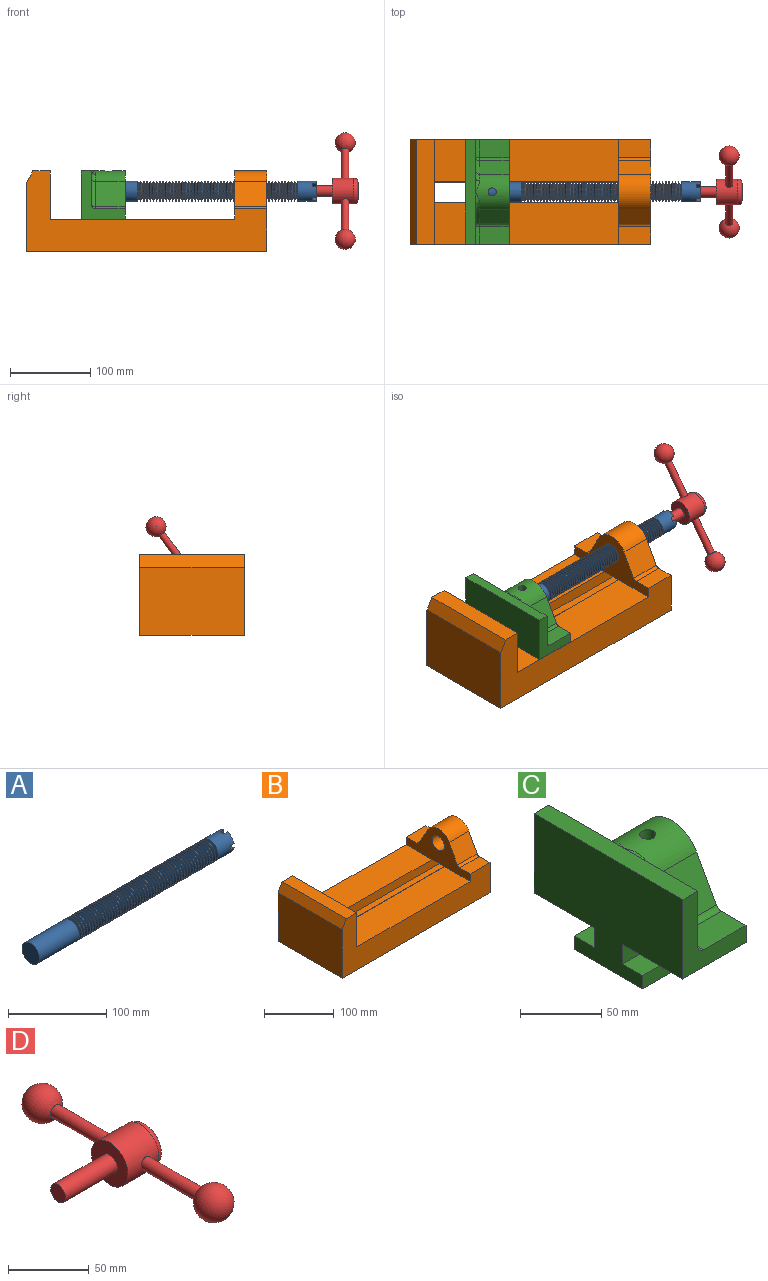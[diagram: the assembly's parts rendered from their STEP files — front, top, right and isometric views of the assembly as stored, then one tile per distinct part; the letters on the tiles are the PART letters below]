
ASSEMBLY  parts=4 mates=3
PART A: 220 faces, bbox 280x25x25 mm
  f0: cylinder r=12.5mm len=25mm, axis (-1,0,0), area 1705.7mm2, adj f1,f2,f3,f54,f57,f208,f209,f210
  f1: plane 9.75x9.75mm, normal (1,0,0), area 59.1mm2, adj f0,f4,f210,f213
  f2: plane 9.75x9.75mm, normal (1,0,0), area 59.1mm2, adj f0,f4,f212,f216
  f3: plane 9.75x9.75mm, normal (1,0,0), area 59.1mm2, adj f0,f4,f209,f218
  f4: cylinder r=6.5mm len=25mm, axis (1,0,0), area 918.4mm2, adj f1,f2,f3,f54,f207,f208,f209,f210
  f5: cylinder r=12.5mm len=25mm, axis (-1,0,0), area 39.3mm2, adj f199,f204
  f6: cylinder r=12.5mm len=25mm, axis (-1,0,0), area 39.3mm2, adj f196,f201
  f7: cylinder r=12.5mm len=25mm, axis (-1,0,0), area 39.3mm2, adj f193,f198
  f8: cylinder r=12.5mm len=25mm, axis (-1,0,0), area 39.3mm2, adj f190,f195
  f9: cylinder r=12.5mm len=25mm, axis (-1,0,0), area 39.3mm2, adj f187,f192
  f10: cylinder r=12.5mm len=25mm, axis (-1,0,0), area 39.3mm2, adj f184,f189
  f11: cylinder r=12.5mm len=25mm, axis (-1,0,0), area 39.3mm2, adj f181,f186
  f12: cylinder r=12.5mm len=25mm, axis (-1,0,0), area 39.3mm2, adj f178,f183
  f13: cylinder r=12.5mm len=25mm, axis (-1,0,0), area 39.3mm2, adj f175,f180
  f14: cylinder r=12.5mm len=25mm, axis (-1,0,0), area 39.3mm2, adj f172,f177
  f15: cylinder r=12.5mm len=25mm, axis (-1,0,0), area 39.3mm2, adj f169,f174
  f16: cylinder r=12.5mm len=25mm, axis (-1,0,0), area 39.3mm2, adj f166,f171
  f17: cylinder r=12.5mm len=25mm, axis (-1,0,0), area 39.3mm2, adj f163,f168
  f18: cylinder r=12.5mm len=25mm, axis (-1,0,0), area 39.3mm2, adj f160,f165
  f19: cylinder r=12.5mm len=25mm, axis (-1,0,0), area 39.3mm2, adj f157,f162
  f20: cylinder r=12.5mm len=25mm, axis (-1,0,0), area 39.3mm2, adj f154,f159
  f21: cylinder r=12.5mm len=25mm, axis (-1,0,0), area 39.3mm2, adj f151,f156
  f22: cylinder r=12.5mm len=25mm, axis (-1,0,0), area 39.3mm2, adj f148,f153
  f23: cylinder r=12.5mm len=25mm, axis (-1,0,0), area 39.3mm2, adj f145,f150
  f24: cylinder r=12.5mm len=25mm, axis (-1,0,0), area 39.3mm2, adj f142,f147
  f25: cylinder r=12.5mm len=25mm, axis (-1,0,0), area 39.3mm2, adj f139,f144
  f26: cylinder r=12.5mm len=25mm, axis (-1,0,0), area 39.3mm2, adj f136,f141
  f27: cylinder r=12.5mm len=25mm, axis (-1,0,0), area 39.3mm2, adj f133,f138
  f28: cylinder r=12.5mm len=25mm, axis (-1,0,0), area 39.3mm2, adj f130,f135
  f29: cylinder r=12.5mm len=25mm, axis (-1,0,0), area 39.3mm2, adj f127,f132
  f30: cylinder r=12.5mm len=25mm, axis (-1,0,0), area 39.3mm2, adj f124,f129
  f31: cylinder r=12.5mm len=25mm, axis (-1,0,0), area 39.3mm2, adj f121,f126
  f32: cylinder r=12.5mm len=25mm, axis (-1,0,0), area 39.3mm2, adj f118,f123
  f33: cylinder r=12.5mm len=25mm, axis (-1,0,0), area 39.3mm2, adj f115,f120
  f34: cylinder r=12.5mm len=25mm, axis (-1,0,0), area 39.3mm2, adj f112,f117
  f35: cylinder r=12.5mm len=25mm, axis (-1,0,0), area 39.3mm2, adj f109,f114
  f36: cylinder r=12.5mm len=25mm, axis (-1,0,0), area 39.3mm2, adj f106,f111
  f37: cylinder r=12.5mm len=25mm, axis (-1,0,0), area 39.3mm2, adj f103,f108
  f38: cylinder r=12.5mm len=25mm, axis (-1,0,0), area 39.3mm2, adj f100,f105
  f39: cylinder r=12.5mm len=25mm, axis (-1,0,0), area 39.3mm2, adj f97,f102
  f40: cylinder r=12.5mm len=25mm, axis (-1,0,0), area 39.3mm2, adj f94,f99
  f41: cylinder r=12.5mm len=25mm, axis (-1,0,0), area 39.3mm2, adj f91,f96
  f42: cylinder r=12.5mm len=25mm, axis (-1,0,0), area 39.3mm2, adj f88,f93
  f43: cylinder r=12.5mm len=25mm, axis (-1,0,0), area 39.3mm2, adj f85,f90
  f44: cylinder r=12.5mm len=25mm, axis (-1,0,0), area 39.3mm2, adj f82,f87
  f45: cylinder r=12.5mm len=25mm, axis (-1,0,0), area 39.3mm2, adj f79,f84
  f46: cylinder r=12.5mm len=25mm, axis (-1,0,0), area 39.3mm2, adj f76,f81
  f47: cylinder r=12.5mm len=25mm, axis (-1,0,0), area 39.3mm2, adj f73,f78
  f48: cylinder r=12.5mm len=25mm, axis (-1,0,0), area 39.3mm2, adj f70,f75
  f49: cylinder r=12.5mm len=25mm, axis (-1,0,0), area 39.3mm2, adj f67,f72
  f50: cylinder r=12.5mm len=25mm, axis (-1,0,0), area 39.3mm2, adj f64,f69
  f51: cylinder r=12.5mm len=25mm, axis (-1,0,0), area 39.3mm2, adj f61,f66
  f52: cylinder r=12.5mm len=25mm, axis (-1,0,0), area 39.3mm2, adj f58,f63
  f53: cylinder r=12.5mm len=25mm, axis (-1,0,0), area 39.3mm2, adj f55,f60
  f54: plane 9.75x9.75mm, normal (1,0,0), area 59.1mm2, adj f0,f4,f215,f217
  f55: cone r=9mm half-angle=71.8deg, axis (-1,0,0), area 248.8mm2, adj f53,f56
  f56: cylinder r=9mm len=18mm, axis (-1,0,0), area 67.9mm2, adj f55,f57
  f57: cone r=12.5mm half-angle=71.8deg, axis (1,0,0), area 248.8mm2, adj f0,f56
  f58: cone r=9mm half-angle=71.8deg, axis (-1,0,0), area 248.8mm2, adj f52,f59
  f59: cylinder r=9mm len=18mm, axis (-1,0,0), area 67.9mm2, adj f58,f60
  f60: cone r=12.5mm half-angle=71.8deg, axis (1,0,0), area 248.8mm2, adj f53,f59
  f61: cone r=9mm half-angle=71.8deg, axis (-1,0,0), area 248.8mm2, adj f51,f62
  f62: cylinder r=9mm len=18mm, axis (-1,0,0), area 67.9mm2, adj f61,f63
  f63: cone r=12.5mm half-angle=71.8deg, axis (1,0,0), area 248.8mm2, adj f52,f62
  f64: cone r=9mm half-angle=71.8deg, axis (-1,0,0), area 248.8mm2, adj f50,f65
  f65: cylinder r=9mm len=18mm, axis (-1,0,0), area 67.9mm2, adj f64,f66
  f66: cone r=12.5mm half-angle=71.8deg, axis (1,0,0), area 248.8mm2, adj f51,f65
  f67: cone r=9mm half-angle=71.8deg, axis (-1,0,0), area 248.8mm2, adj f49,f68
  f68: cylinder r=9mm len=18mm, axis (-1,0,0), area 67.9mm2, adj f67,f69
  f69: cone r=12.5mm half-angle=71.8deg, axis (1,0,0), area 248.8mm2, adj f50,f68
  f70: cone r=9mm half-angle=71.8deg, axis (-1,0,0), area 248.8mm2, adj f48,f71
  f71: cylinder r=9mm len=18mm, axis (-1,0,0), area 67.9mm2, adj f70,f72
  f72: cone r=12.5mm half-angle=71.8deg, axis (1,0,0), area 248.8mm2, adj f49,f71
  f73: cone r=9mm half-angle=71.8deg, axis (-1,0,0), area 248.8mm2, adj f47,f74
  f74: cylinder r=9mm len=18mm, axis (-1,0,0), area 67.9mm2, adj f73,f75
  f75: cone r=12.5mm half-angle=71.8deg, axis (1,0,0), area 248.8mm2, adj f48,f74
  f76: cone r=9mm half-angle=71.8deg, axis (-1,0,0), area 248.8mm2, adj f46,f77
  f77: cylinder r=9mm len=18mm, axis (-1,0,0), area 67.9mm2, adj f76,f78
  f78: cone r=12.5mm half-angle=71.8deg, axis (1,0,0), area 248.8mm2, adj f47,f77
  f79: cone r=9mm half-angle=71.8deg, axis (-1,0,0), area 248.8mm2, adj f45,f80
  f80: cylinder r=9mm len=18mm, axis (-1,0,0), area 67.9mm2, adj f79,f81
  f81: cone r=12.5mm half-angle=71.8deg, axis (1,0,0), area 248.8mm2, adj f46,f80
  f82: cone r=9mm half-angle=71.8deg, axis (-1,0,0), area 248.8mm2, adj f44,f83
  f83: cylinder r=9mm len=18mm, axis (-1,0,0), area 67.9mm2, adj f82,f84
  f84: cone r=12.5mm half-angle=71.8deg, axis (1,0,0), area 248.8mm2, adj f45,f83
  f85: cone r=9mm half-angle=71.8deg, axis (-1,0,0), area 248.8mm2, adj f43,f86
  f86: cylinder r=9mm len=18mm, axis (-1,0,0), area 67.9mm2, adj f85,f87
  f87: cone r=12.5mm half-angle=71.8deg, axis (1,0,0), area 248.8mm2, adj f44,f86
  f88: cone r=9mm half-angle=71.8deg, axis (-1,0,0), area 248.8mm2, adj f42,f89
  f89: cylinder r=9mm len=18mm, axis (-1,0,0), area 67.9mm2, adj f88,f90
  f90: cone r=12.5mm half-angle=71.8deg, axis (1,0,0), area 248.8mm2, adj f43,f89
  f91: cone r=9mm half-angle=71.8deg, axis (-1,0,0), area 248.8mm2, adj f41,f92
  f92: cylinder r=9mm len=18mm, axis (-1,0,0), area 67.9mm2, adj f91,f93
  f93: cone r=12.5mm half-angle=71.8deg, axis (1,0,0), area 248.8mm2, adj f42,f92
  f94: cone r=9mm half-angle=71.8deg, axis (-1,0,0), area 248.8mm2, adj f40,f95
  f95: cylinder r=9mm len=18mm, axis (-1,0,0), area 67.9mm2, adj f94,f96
  f96: cone r=12.5mm half-angle=71.8deg, axis (1,0,0), area 248.8mm2, adj f41,f95
  f97: cone r=9mm half-angle=71.8deg, axis (-1,0,0), area 248.8mm2, adj f39,f98
  f98: cylinder r=9mm len=18mm, axis (-1,0,0), area 67.9mm2, adj f97,f99
  f99: cone r=12.5mm half-angle=71.8deg, axis (1,0,0), area 248.8mm2, adj f40,f98
  f100: cone r=9mm half-angle=71.8deg, axis (-1,0,0), area 248.8mm2, adj f38,f101
  f101: cylinder r=9mm len=18mm, axis (-1,0,0), area 67.9mm2, adj f100,f102
  f102: cone r=12.5mm half-angle=71.8deg, axis (1,0,0), area 248.8mm2, adj f39,f101
  f103: cone r=9mm half-angle=71.8deg, axis (-1,0,0), area 248.8mm2, adj f37,f104
  f104: cylinder r=9mm len=18mm, axis (-1,0,0), area 67.9mm2, adj f103,f105
  f105: cone r=12.5mm half-angle=71.8deg, axis (1,0,0), area 248.8mm2, adj f38,f104
  f106: cone r=9mm half-angle=71.8deg, axis (-1,0,0), area 248.8mm2, adj f36,f107
  f107: cylinder r=9mm len=18mm, axis (-1,0,0), area 67.9mm2, adj f106,f108
  f108: cone r=12.5mm half-angle=71.8deg, axis (1,0,0), area 248.8mm2, adj f37,f107
  f109: cone r=9mm half-angle=71.8deg, axis (-1,0,0), area 248.8mm2, adj f35,f110
  f110: cylinder r=9mm len=18mm, axis (-1,0,0), area 67.9mm2, adj f109,f111
  f111: cone r=12.5mm half-angle=71.8deg, axis (1,0,0), area 248.8mm2, adj f36,f110
  f112: cone r=9mm half-angle=71.8deg, axis (-1,0,0), area 248.8mm2, adj f34,f113
  f113: cylinder r=9mm len=18mm, axis (-1,0,0), area 67.9mm2, adj f112,f114
  f114: cone r=12.5mm half-angle=71.8deg, axis (1,0,0), area 248.8mm2, adj f35,f113
  f115: cone r=9mm half-angle=71.8deg, axis (-1,0,0), area 248.8mm2, adj f33,f116
  f116: cylinder r=9mm len=18mm, axis (-1,0,0), area 67.9mm2, adj f115,f117
  f117: cone r=12.5mm half-angle=71.8deg, axis (1,0,0), area 248.8mm2, adj f34,f116
  f118: cone r=9mm half-angle=71.8deg, axis (-1,0,0), area 248.8mm2, adj f32,f119
  f119: cylinder r=9mm len=18mm, axis (-1,0,0), area 67.9mm2, adj f118,f120
  f120: cone r=12.5mm half-angle=71.8deg, axis (1,0,0), area 248.8mm2, adj f33,f119
  f121: cone r=9mm half-angle=71.8deg, axis (-1,0,0), area 248.8mm2, adj f31,f122
  f122: cylinder r=9mm len=18mm, axis (-1,0,0), area 67.9mm2, adj f121,f123
  f123: cone r=12.5mm half-angle=71.8deg, axis (1,0,0), area 248.8mm2, adj f32,f122
  f124: cone r=9mm half-angle=71.8deg, axis (-1,0,0), area 248.8mm2, adj f30,f125
  f125: cylinder r=9mm len=18mm, axis (-1,0,0), area 67.9mm2, adj f124,f126
  f126: cone r=12.5mm half-angle=71.8deg, axis (1,0,0), area 248.8mm2, adj f31,f125
  f127: cone r=9mm half-angle=71.8deg, axis (-1,0,0), area 248.8mm2, adj f29,f128
  f128: cylinder r=9mm len=18mm, axis (-1,0,0), area 67.9mm2, adj f127,f129
  f129: cone r=12.5mm half-angle=71.8deg, axis (1,0,0), area 248.8mm2, adj f30,f128
  f130: cone r=9mm half-angle=71.8deg, axis (-1,0,0), area 248.8mm2, adj f28,f131
  f131: cylinder r=9mm len=18mm, axis (-1,0,0), area 67.9mm2, adj f130,f132
  f132: cone r=12.5mm half-angle=71.8deg, axis (1,0,0), area 248.8mm2, adj f29,f131
  f133: cone r=9mm half-angle=71.8deg, axis (-1,0,0), area 248.8mm2, adj f27,f134
  f134: cylinder r=9mm len=18mm, axis (-1,0,0), area 67.9mm2, adj f133,f135
  f135: cone r=12.5mm half-angle=71.8deg, axis (1,0,0), area 248.8mm2, adj f28,f134
  f136: cone r=9mm half-angle=71.8deg, axis (-1,0,0), area 248.8mm2, adj f26,f137
  f137: cylinder r=9mm len=18mm, axis (-1,0,0), area 67.9mm2, adj f136,f138
  f138: cone r=12.5mm half-angle=71.8deg, axis (1,0,0), area 248.8mm2, adj f27,f137
  f139: cone r=9mm half-angle=71.8deg, axis (-1,0,0), area 248.8mm2, adj f25,f140
  f140: cylinder r=9mm len=18mm, axis (-1,0,0), area 67.9mm2, adj f139,f141
  f141: cone r=12.5mm half-angle=71.8deg, axis (1,0,0), area 248.8mm2, adj f26,f140
  f142: cone r=9mm half-angle=71.8deg, axis (-1,0,0), area 248.8mm2, adj f24,f143
  f143: cylinder r=9mm len=18mm, axis (-1,0,0), area 67.9mm2, adj f142,f144
  f144: cone r=12.5mm half-angle=71.8deg, axis (1,0,0), area 248.8mm2, adj f25,f143
  f145: cone r=9mm half-angle=71.8deg, axis (-1,0,0), area 248.8mm2, adj f23,f146
  f146: cylinder r=9mm len=18mm, axis (-1,0,0), area 67.9mm2, adj f145,f147
  f147: cone r=12.5mm half-angle=71.8deg, axis (1,0,0), area 248.8mm2, adj f24,f146
  f148: cone r=9mm half-angle=71.8deg, axis (-1,0,0), area 248.8mm2, adj f22,f149
  f149: cylinder r=9mm len=18mm, axis (-1,0,0), area 67.9mm2, adj f148,f150
  f150: cone r=12.5mm half-angle=71.8deg, axis (1,0,0), area 248.8mm2, adj f23,f149
  f151: cone r=9mm half-angle=71.8deg, axis (-1,0,0), area 248.8mm2, adj f21,f152
  f152: cylinder r=9mm len=18mm, axis (-1,0,0), area 67.9mm2, adj f151,f153
  f153: cone r=12.5mm half-angle=71.8deg, axis (1,0,0), area 248.8mm2, adj f22,f152
  f154: cone r=9mm half-angle=71.8deg, axis (-1,0,0), area 248.8mm2, adj f20,f155
  f155: cylinder r=9mm len=18mm, axis (-1,0,0), area 67.9mm2, adj f154,f156
  f156: cone r=12.5mm half-angle=71.8deg, axis (1,0,0), area 248.8mm2, adj f21,f155
  f157: cone r=9mm half-angle=71.8deg, axis (-1,0,0), area 248.8mm2, adj f19,f158
  f158: cylinder r=9mm len=18mm, axis (-1,0,0), area 67.9mm2, adj f157,f159
  f159: cone r=12.5mm half-angle=71.8deg, axis (1,0,0), area 248.8mm2, adj f20,f158
  f160: cone r=9mm half-angle=71.8deg, axis (-1,0,0), area 248.8mm2, adj f18,f161
  f161: cylinder r=9mm len=18mm, axis (-1,0,0), area 67.9mm2, adj f160,f162
  f162: cone r=12.5mm half-angle=71.8deg, axis (1,0,0), area 248.8mm2, adj f19,f161
  f163: cone r=9mm half-angle=71.8deg, axis (-1,0,0), area 248.8mm2, adj f17,f164
  f164: cylinder r=9mm len=18mm, axis (-1,0,0), area 67.9mm2, adj f163,f165
  f165: cone r=12.5mm half-angle=71.8deg, axis (1,0,0), area 248.8mm2, adj f18,f164
  f166: cone r=9mm half-angle=71.8deg, axis (-1,0,0), area 248.8mm2, adj f16,f167
  f167: cylinder r=9mm len=18mm, axis (-1,0,0), area 67.9mm2, adj f166,f168
  f168: cone r=12.5mm half-angle=71.8deg, axis (1,0,0), area 248.8mm2, adj f17,f167
  f169: cone r=9mm half-angle=71.8deg, axis (-1,0,0), area 248.8mm2, adj f15,f170
  f170: cylinder r=9mm len=18mm, axis (-1,0,0), area 67.9mm2, adj f169,f171
  f171: cone r=12.5mm half-angle=71.8deg, axis (1,0,0), area 248.8mm2, adj f16,f170
  f172: cone r=9mm half-angle=71.8deg, axis (-1,0,0), area 248.8mm2, adj f14,f173
  f173: cylinder r=9mm len=18mm, axis (-1,0,0), area 67.9mm2, adj f172,f174
  f174: cone r=12.5mm half-angle=71.8deg, axis (1,0,0), area 248.8mm2, adj f15,f173
  f175: cone r=9mm half-angle=71.8deg, axis (-1,0,0), area 248.8mm2, adj f13,f176
  f176: cylinder r=9mm len=18mm, axis (-1,0,0), area 67.9mm2, adj f175,f177
  f177: cone r=12.5mm half-angle=71.8deg, axis (1,0,0), area 248.8mm2, adj f14,f176
  f178: cone r=9mm half-angle=71.8deg, axis (-1,0,0), area 248.8mm2, adj f12,f179
  f179: cylinder r=9mm len=18mm, axis (-1,0,0), area 67.9mm2, adj f178,f180
  f180: cone r=12.5mm half-angle=71.8deg, axis (1,0,0), area 248.8mm2, adj f13,f179
  f181: cone r=9mm half-angle=71.8deg, axis (-1,0,0), area 248.8mm2, adj f11,f182
  f182: cylinder r=9mm len=18mm, axis (-1,0,0), area 67.9mm2, adj f181,f183
  f183: cone r=12.5mm half-angle=71.8deg, axis (1,0,0), area 248.8mm2, adj f12,f182
  f184: cone r=9mm half-angle=71.8deg, axis (-1,0,0), area 248.8mm2, adj f10,f185
  f185: cylinder r=9mm len=18mm, axis (-1,0,0), area 67.9mm2, adj f184,f186
  f186: cone r=12.5mm half-angle=71.8deg, axis (1,0,0), area 248.8mm2, adj f11,f185
  f187: cone r=9mm half-angle=71.8deg, axis (-1,0,0), area 248.8mm2, adj f9,f188
  f188: cylinder r=9mm len=18mm, axis (-1,0,0), area 67.9mm2, adj f187,f189
  f189: cone r=12.5mm half-angle=71.8deg, axis (1,0,0), area 248.8mm2, adj f10,f188
  f190: cone r=9mm half-angle=71.8deg, axis (-1,0,0), area 248.8mm2, adj f8,f191
  f191: cylinder r=9mm len=18mm, axis (-1,0,0), area 67.9mm2, adj f190,f192
  f192: cone r=12.5mm half-angle=71.8deg, axis (1,0,0), area 248.8mm2, adj f9,f191
  f193: cone r=9mm half-angle=71.8deg, axis (-1,0,0), area 248.8mm2, adj f7,f194
  f194: cylinder r=9mm len=18mm, axis (-1,0,0), area 67.9mm2, adj f193,f195
  f195: cone r=12.5mm half-angle=71.8deg, axis (1,0,0), area 248.8mm2, adj f8,f194
  f196: cone r=9mm half-angle=71.8deg, axis (-1,0,0), area 248.8mm2, adj f6,f197
  f197: cylinder r=9mm len=18mm, axis (-1,0,0), area 67.9mm2, adj f196,f198
  f198: cone r=12.5mm half-angle=71.8deg, axis (1,0,0), area 248.8mm2, adj f7,f197
  f199: cone r=9mm half-angle=71.8deg, axis (-1,0,0), area 248.8mm2, adj f5,f200
  f200: cylinder r=9mm len=18mm, axis (-1,0,0), area 67.9mm2, adj f199,f201
  f201: cone r=12.5mm half-angle=71.8deg, axis (1,0,0), area 248.8mm2, adj f6,f200
  f202: cone r=9mm half-angle=71.8deg, axis (-1,0,0), area 248.8mm2, adj f203,f206
  f203: cylinder r=9mm len=18mm, axis (-1,0,0), area 67.9mm2, adj f202,f204
  f204: cone r=12.5mm half-angle=71.8deg, axis (1,0,0), area 248.8mm2, adj f5,f203
  f205: plane 25x25mm, normal (-1,0,0), area 490.9mm2, adj f206
  f206: cylinder r=12.5mm len=57.5mm, axis (-1,0,0), area 4516mm2, adj f202,f205
  f207: plane 13x13mm, normal (1,0,0), area 132.7mm2, adj f4
  f208: plane 6.5x5mm, normal (1,0,0), area 30.4mm2, adj f0,f4,f209,f210
  f209: plane 6.25x5mm, normal (0,1,0), area 31.2mm2, adj f0,f3,f4,f208
  f210: plane 6.25x5mm, normal (0,-1,0), area 31.2mm2, adj f0,f1,f4,f208
  f211: plane 6.5x5mm, normal (1,0,0), area 30.4mm2, adj f0,f4,f212,f213
  f212: plane 6.25x5mm, normal (0,0,-1), area 31.2mm2, adj f0,f2,f4,f211
  f213: plane 6.25x5mm, normal (0,0,1), area 31.2mm2, adj f0,f1,f4,f211
  f214: plane 6.5x5mm, normal (1,0,0), area 30.4mm2, adj f0,f4,f215,f216
  f215: plane 6.25x5mm, normal (0,1,0), area 31.2mm2, adj f0,f4,f54,f214
  f216: plane 6.25x5mm, normal (0,-1,0), area 31.2mm2, adj f0,f2,f4,f214
  f217: plane 6.25x5mm, normal (0,0,-1), area 31.2mm2, adj f0,f4,f54,f219
  f218: plane 6.25x5mm, normal (0,0,1), area 31.2mm2, adj f0,f3,f4,f219
  f219: plane 6.5x5mm, normal (1,0,0), area 30.4mm2, adj f0,f4,f217,f218
PART B: 30 faces, bbox 300x130x100 mm
  f0: plane 230x52.5mm, normal (0,0,1), area 12075mm2, adj f4,f7,f16,f24
  f1: plane 300x130mm, normal (0,0,-1), area 32250mm2, adj f2,f4,f6,f7,f8,f18,f19
  f2: plane 130x100mm, normal (1,0,0), area 7577.9mm2, adj f1,f7,f8,f10,f11,f12,f13,f14
  f3: plane 230x52.5mm, normal (0,0,1), area 12075mm2, adj f4,f8,f16,f23
  f4: plane 130x100mm, normal (1,0,0), area 9150mm2, adj f0,f1,f3,f5,f7,f8,f18,f19
  f5: plane 130x21.34mm, normal (0,0,1), area 2774.2mm2, adj f4,f7,f8,f9
  f6: plane 130x85mm, normal (-1,0,0), area 11050mm2, adj f1,f7,f8,f9
  f7: plane 300x100mm, normal (0,-1,0), area 14255mm2, adj f0,f1,f2,f4,f5,f6,f9,f14
  f8: plane 300x100mm, normal (0,1,0), area 14255mm2, adj f1,f2,f3,f4,f5,f6,f9,f10
  f9: plane 130x15mm, normal (-0.87,0,0.5), area 2251.7mm2, adj f5,f6,f7,f8
  f10: plane 40x21.6mm, normal (0,0,1), area 864mm2, adj f2,f8,f16,f28
  f11: plane 40x31.34mm, normal (0,0.88,0.48), area 1426.9mm2, adj f2,f12,f16,f28
  f12: cylinder r=25mm len=43.92mm, axis (1,0,0), area 2145.1mm2, adj f2,f11,f13,f16
  f13: plane 40x31.34mm, normal (0,-0.88,0.48), area 1426.9mm2, adj f2,f12,f16,f29
  f14: plane 40x21.6mm, normal (0,0,1), area 864mm2, adj f2,f7,f16,f29
  f15: cylinder r=12.5mm len=40mm, axis (1,0,0), area 3141.6mm2, adj f2,f16
  f16: plane 130x60mm, normal (-1,0,0), area 3727.9mm2, adj f0,f3,f7,f8,f10,f11,f12,f13
  f17: plane 40x25mm, normal (0,0,-1), area 1000mm2, adj f2,f16,f23,f24
  f18: plane 270x15mm, normal (0,1,0), area 4050mm2, adj f1,f2,f4,f25
  f19: plane 270x15mm, normal (0,-1,0), area 4050mm2, adj f1,f2,f4,f20
  f20: plane 270x17.5mm, normal (0,0,1), area 4725mm2, adj f2,f4,f19,f21
  f21: plane 270x10mm, normal (0,-1,0), area 2700mm2, adj f2,f4,f20,f22
  f22: plane 270x17.5mm, normal (0,0,-1), area 4725mm2, adj f2,f4,f21,f23
  f23: plane 270x15mm, normal (0,-1,0), area 4050mm2, adj f2,f3,f4,f17,f22
  f24: plane 270x15mm, normal (0,1,0), area 4050mm2, adj f0,f2,f4,f17,f26
  f25: plane 270x17.5mm, normal (0,0,1), area 4725mm2, adj f2,f4,f18,f27
  f26: plane 270x17.5mm, normal (0,0,-1), area 4725mm2, adj f2,f4,f24,f27
  f27: plane 270x10mm, normal (0,1,0), area 2700mm2, adj f2,f4,f25,f26
  f28: cylinder r=5mm len=40mm, axis (-1,0,0), area 214.5mm2, adj f2,f10,f11,f16
  f29: cylinder r=5mm len=40mm, axis (1,0,0), area 214.5mm2, adj f2,f13,f14,f16
PART C: 36 faces, bbox 55.4x130.4x90.6 mm
  f0: cylinder r=12.5mm len=42mm, axis (-1,0,0), area 3218.6mm2, adj f5,f15,f23
  f1: plane 55x52.5mm, normal (0,0,-1), area 2887.5mm2, adj f4,f5,f11,f16
  f2: plane 37x21.6mm, normal (0,0,1), area 799.2mm2, adj f4,f5,f24,f25
  f3: plane 48.42x42mm, normal (1,0,0), area 1399.6mm2, adj f8,f10,f31,f33,f34
  f4: plane 60x55mm, normal (0,1,0), area 1331.4mm2, adj f1,f2,f5,f7,f10,f11,f24
  f5: plane 130x85mm, normal (1,0,0), area 4702.9mm2, adj f0,f1,f2,f4,f6,f8,f9,f12
  f6: plane 37x21.6mm, normal (0,0,1), area 799.2mm2, adj f5,f8,f30,f31
  f7: plane 48.42x42mm, normal (1,0,0), area 1399.6mm2, adj f4,f10,f24,f28,f29
  f8: plane 60x55mm, normal (0,-1,0), area 1331.4mm2, adj f3,f5,f6,f9,f10,f11,f31
  f9: plane 55x52.5mm, normal (0,0,-1), area 2887.5mm2, adj f5,f8,f11,f17
  f10: plane 130.35x13.35mm, normal (0,0,1), area 1690mm2, adj f3,f4,f7,f8,f11,f26,f35
  f11: plane 130x85mm, normal (-1,0,0), area 8775mm2, adj f1,f4,f8,f9,f10,f16,f17,f18
  f12: plane 37x31.34mm, normal (0,0.88,0.48), area 1319.9mm2, adj f5,f13,f25,f29
  f13: cylinder r=25mm len=43.92mm, axis (-1,0,0), area 1962.1mm2, adj f5,f12,f14,f23,f26,f28,f34,f35
  f14: plane 37x31.34mm, normal (0,-0.88,0.48), area 1319.9mm2, adj f5,f13,f30,f33
  f15: plane 25x25mm, normal (1,0,0), area 490.9mm2, adj f0
  f16: plane 55x15mm, normal (0,1,0), area 825mm2, adj f1,f5,f11,f22
  f17: plane 55x15mm, normal (0,-1,0), area 825mm2, adj f5,f9,f11,f18
  f18: plane 55x17.5mm, normal (0,0,1), area 962.5mm2, adj f5,f11,f17,f19
  f19: plane 55x10mm, normal (0,-1,0), area 550mm2, adj f5,f11,f18,f20
  f20: plane 60x55mm, normal (0,0,-1), area 3300mm2, adj f5,f11,f19,f21
  f21: plane 55x10mm, normal (0,1,0), area 550mm2, adj f5,f11,f20,f22
  f22: plane 55x17.5mm, normal (0,0,1), area 962.5mm2, adj f5,f11,f16,f21
  f23: cylinder r=5mm len=13.54mm, axis (0,0,1), area 401mm2, adj f0,f13
  f24: cylinder r=5mm len=21.6mm, axis (0,1,0), area 169.6mm2, adj f2,f4,f7,f27
  f25: cylinder r=5mm len=37mm, axis (1,0,0), area 198.4mm2, adj f2,f5,f12,f27
  f26: bspline ~17.21x5.35mm, area 55.9mm2, adj f10,f13,f28
  f27: sphere r=5mm, area 26.8mm2, adj f24,f25,f29
  f28: torus R=30mm, axis (-1,0,0), area 102.5mm2, adj f7,f13,f26,f29
  f29: cylinder r=5mm len=33.73mm, axis (0,0.48,-0.88), area 280.2mm2, adj f7,f12,f27,f28
  f30: cylinder r=5mm len=37mm, axis (1,0,0), area 198.4mm2, adj f5,f6,f14,f32
  f31: cylinder r=5mm len=21.6mm, axis (0,1,0), area 169.6mm2, adj f3,f6,f8,f32
  f32: sphere r=5mm, area 26.8mm2, adj f30,f31,f33
  f33: cylinder r=5mm len=33.73mm, axis (0,0.48,0.88), area 280.2mm2, adj f3,f14,f32,f34
  f34: torus R=30mm, axis (-1,0,0), area 102.5mm2, adj f3,f13,f33,f35
  f35: bspline ~17.21x5.35mm, area 55.9mm2, adj f10,f13,f34
PART D: 10 faces, bbox 77x175x34.6 mm
  f0: cylinder r=4.5mm len=47.97mm, axis (0,1,0), area 1347.1mm2, adj f2,f8
  f1: cylinder r=4.5mm len=47.97mm, axis (0,1,0), area 1347.1mm2, adj f2,f7
  f2: cylinder r=16mm len=32mm, axis (-1,0,0), area 2585.9mm2, adj f0,f1,f6,f9
  f3: cylinder r=6.5mm len=45mm, axis (-1,0,0), area 1837.8mm2, adj f4,f6
  f4: plane 13x13mm, normal (-1,0,0), area 132.7mm2, adj f3
  f5: plane 22x22mm, normal (1,0,0), area 380.1mm2, adj f9
  f6: plane 32x32mm, normal (-1,0,0), area 671.5mm2, adj f2,f3
  f7: sphere r=12.52mm, area 1902.6mm2, adj f1
  f8: sphere r=12.52mm, area 1902.6mm2, adj f0
  f9: torus R=11mm, axis (1,0,0), area 699.9mm2, adj f2,f5
PLACE A rot(axis=(1,0,0),53.3deg) t=(38.52,60.15,30.2)mm
PLACE B at identity fixed
PLACE C t=(38.52,0,0)mm
PLACE D rot(axis=(1,0,0),53.3deg) t=(38.52,60.15,30.2)mm
MATE revolute A.f0 <-> C.f28  axis (-1,0,0) through (-218.48,0,75)mm
MATE fastened D.f2 <-> A.f0  axis (-1,0,0) through (36.52,0,75)mm
MATE slider C.f11 <-> B.f4  axis (-1,0,0) through (-231.48,-65,40)mm
